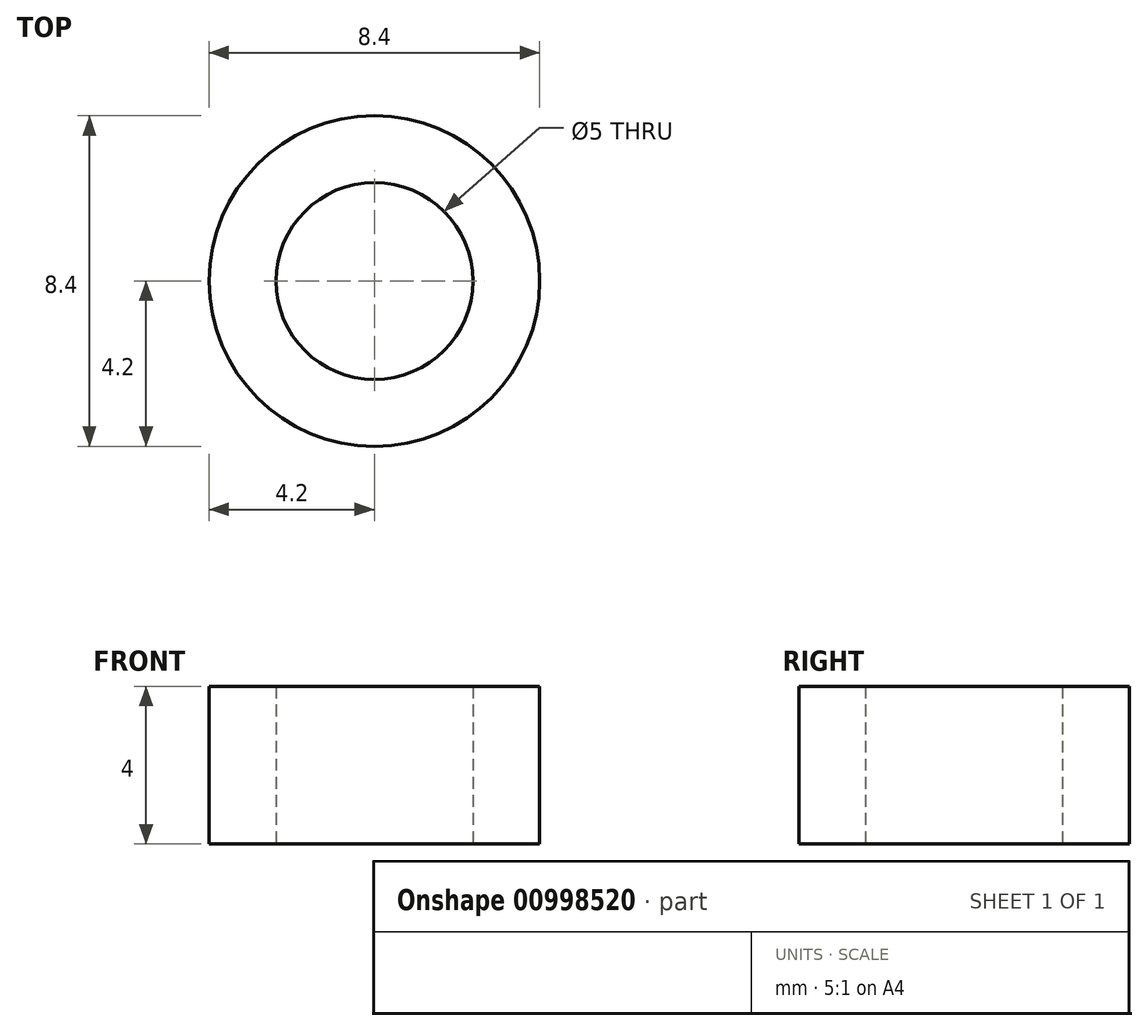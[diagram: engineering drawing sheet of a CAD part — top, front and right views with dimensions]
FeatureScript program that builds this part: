
annotation { "Feature Type Name" : "Feature", "Feature Type Description" : "" }
export const myFeature = defineFeature(function(context is Context, id is Id, definition is map)
    precondition{}
    {
        {
            var Q0;
            Q0=qCreatedBy(makeId("Top.planeOp"),FACE);
            var sketch = newSketch(context, id + "F0", { "sketchPlane" : qUnion([Q0])});
            skCircle(sketch, "E0", {"center": v(0, 0) * mm, "radius": 2.5 * mm});
            skCircle(sketch, "E1", {"center": v(0, 0) * mm, "radius": 4.2 * mm});
            skSolve(sketch);
        }
        {
            var Q0;
            Q0 = qSketchRegion(id + "F0", true);
            extrude(context, id + "F1", {"entities" : qUnion([Q0]), "depth" : 4 * mm, "offsetDistance" : 25 * mm});
        }
    });
